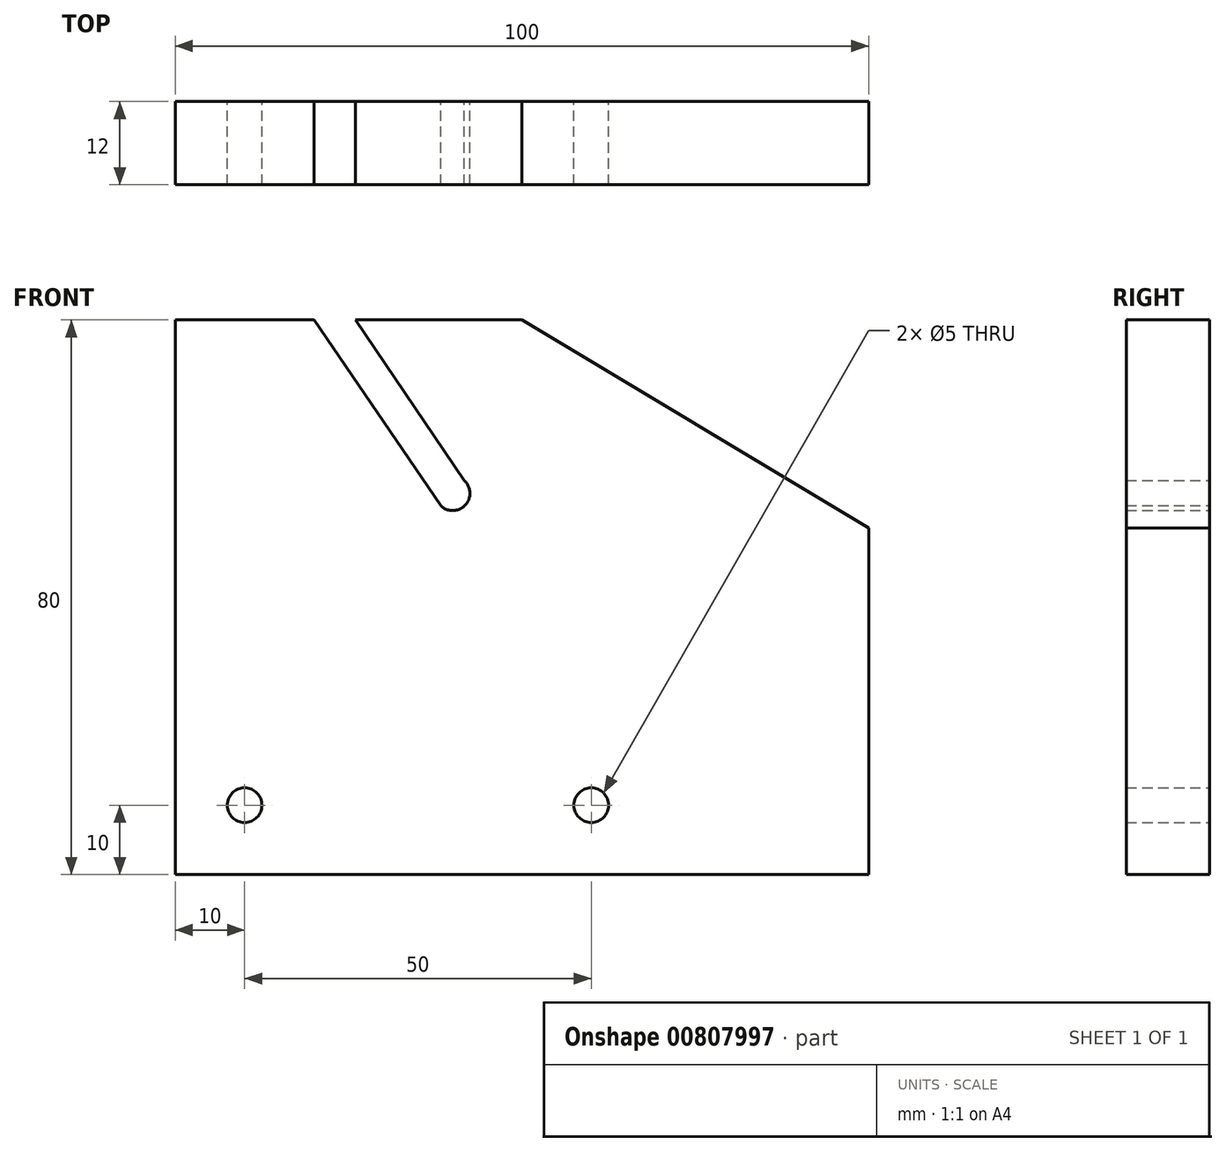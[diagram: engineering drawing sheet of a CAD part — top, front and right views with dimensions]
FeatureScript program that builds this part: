
annotation { "Feature Type Name" : "Feature", "Feature Type Description" : "" }
export const myFeature = defineFeature(function(context is Context, id is Id, definition is map)
    precondition{}
    {
        {
            var Q0;
            Q0=qCreatedBy(makeId("Front.planeOp"),FACE);
            var sketch = newSketch(context, id + "F0", { "sketchPlane" : qUnion([Q0])});
            skLineSegment(sketch, "E0.bottom", {"start": v(0, 0) * mm, "end": v(100, 0) * mm});
            skLineSegment(sketch, "E0.top", {"start": v(0, 80) * mm, "end": v(20, 80) * mm});
            skLineSegment(sketch, "E0.left", {"start": v(0, 0) * mm, "end": v(0, 80) * mm});
            skLineSegment(sketch, "E0.right", {"start": v(100, 0) * mm, "end": v(100, 50) * mm});
            skLineSegment(sketch, "E1", {"start": v(50, 80) * mm, "end": v(100, 50) * mm});
            skPoint(sketch, "E2.orphan", {"position": v(100, 80) * mm});
            skArc(sketch, "E3", {"start": v(38.27, 53.2) * mm, "mid": v(41.82, 53.3) * mm, "end": v(41.7, 56.84) * mm});
            skLineSegment(sketch, "E4", {"start": v(41.7, 56.84) * mm, "end": v(26, 80) * mm});
            skLineSegment(sketch, "E5", {"start": v(37.69, 54.06) * mm, "end": v(20, 80) * mm});
            skLineSegment(sketch, "E6.trimOffspring", {"start": v(26, 80) * mm, "end": v(50, 80) * mm});
            skCircle(sketch, "E7", {"center": v(10, 10) * mm, "radius": 2.5 * mm});
            skCircle(sketch, "E8", {"center": v(60, 10) * mm, "radius": 2.5 * mm});
            skLineSegment(sketch, "E9", {"start": v(38.27, 53.2) * mm, "end": v(37.69, 54.06) * mm});
            skSolve(sketch);
        }
        {
            var Q0;
            Q0 = qSketchRegion(id + "F0", true);
            extrude(context, id + "F1", {"entities" : qUnion([Q0]), "depth" : 12 * mm, "offsetDistance" : 25 * mm});
        }
    });
